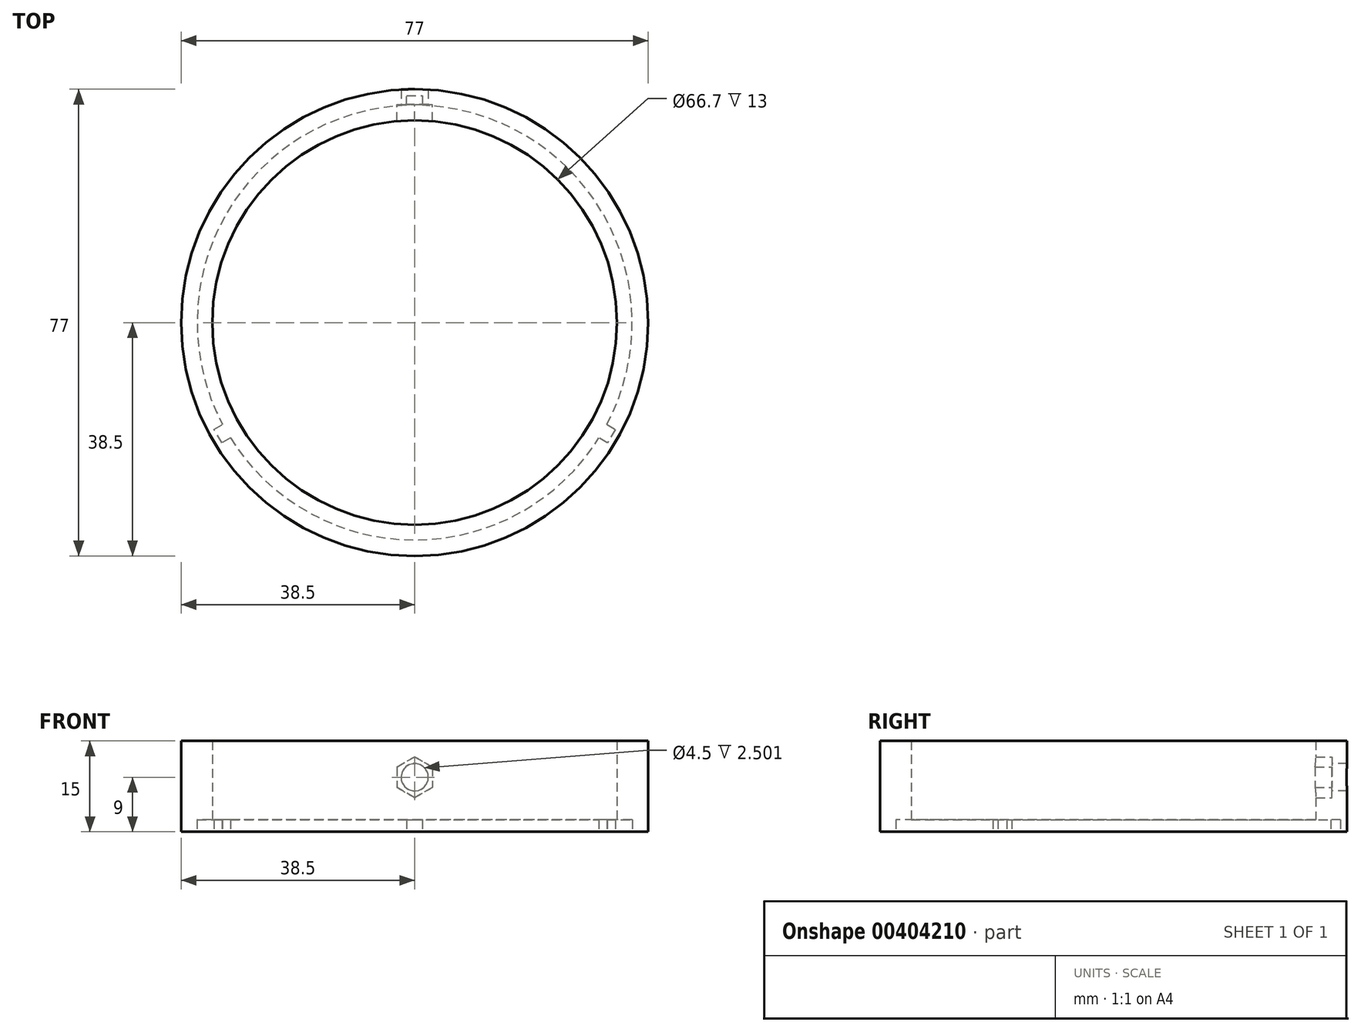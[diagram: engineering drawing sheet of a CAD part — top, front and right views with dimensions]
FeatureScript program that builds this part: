
annotation { "Feature Type Name" : "Feature", "Feature Type Description" : "" }
export const myFeature = defineFeature(function(context is Context, id is Id, definition is map)
    precondition{}
    {
        {
            var Q0;
            Q0=qCreatedBy(makeId("Top.planeOp"),FACE);
            var sketch = newSketch(context, id + "F0", { "sketchPlane" : qUnion([Q0])});
            skCircle(sketch, "E0", {"center": v(0, 0) * mm, "radius": 33.35 * mm});
            skCircle(sketch, "E1", {"center": v(0, 0) * mm, "radius": 38.5 * mm});
            skSolve(sketch);
        }
        {
            var Q0;
            Q0=qSketchRegion(id+"F0",true);
            extrude(context, id + "F1", {"entities" : qUnion([Q0]), "depth" : 15 * mm});
        }
        {
            var Q0;
            Q0=qCreatedBy(makeId("Front.planeOp"),FACE);
            var sketch = newSketch(context, id + "F2", { "sketchPlane" : qUnion([Q0])});
            skCircle(sketch, "E2", {"center": v(0, 9) * mm, "radius": 2.25 * mm});
            skSolve(sketch);
        }
        {
            var Q0;
            Q0=qSketchRegion(id+"F2",true);
            extrude(context, id + "F3", {"entities" : qUnion([Q0]), "operationType" : NewBodyOperationType.REMOVE, "endBound" : BoundingType.THROUGH_ALL, "oppositeDirection" : true, "depth" : 25 * mm});
        }
        {
            var Q0;
            Q0=qCreatedBy(makeId("Front.planeOp"),FACE);
            cPlane(context, id + "F4", {"entities" : qUnion([Q0]), "cplaneType" : CPlaneType.OFFSET, "offset" : 36 * mm, "oppositeDirection" : true, "width" : 150 * mm, "height" : 150 * mm});
        }
        {
            var Q0;
            Q0=qCreatedBy(id+"F4.planeOp",FACE);
            var sketch = newSketch(context, id + "F5", { "sketchPlane" : qUnion([Q0])});
            skCircle(sketch, "E3.cCircle", {"center": v(0, 9) * mm, "radius": 2.92 * mm, "construction": true});
            skLineSegment(sketch, "E3.0", {"start": v(2.92, 10.68) * mm, "end": v(2.92, 7.32) * mm});
            skLineSegment(sketch, "E3.1", {"start": v(2.92, 7.32) * mm, "end": v(0, 5.63) * mm});
            skLineSegment(sketch, "E3.2", {"start": v(0, 5.63) * mm, "end": v(-2.92, 7.32) * mm});
            skLineSegment(sketch, "E3.3", {"start": v(-2.92, 7.32) * mm, "end": v(-2.92, 10.68) * mm});
            skLineSegment(sketch, "E3.4", {"start": v(-2.92, 10.68) * mm, "end": v(0, 12.37) * mm});
            skLineSegment(sketch, "E3.5", {"start": v(0, 12.37) * mm, "end": v(2.92, 10.68) * mm});
            skPoint(sketch, "E3.0.midPoint", {"position": v(2.92, 9) * mm});
            skSolve(sketch);
        }
        {
            var Q0;
            Q0=qSketchRegion(id+"F5",true);
            extrude(context, id + "F6", {"entities" : qUnion([Q0]), "operationType" : NewBodyOperationType.REMOVE, "depth" : 4 * mm});
        }
        {
            var Q0;
            Q0=makeQuery(id+"F1.opExtrude","CAP_FACE",FACE,{"disambiguationData":[OSD([sQuery(id+"F0.wireOp",EDGE,"E0"),sQuery(id+"F0.wireOp",EDGE,"E1")])],"isStart":false});
            var sketch = newSketch(context, id + "F7", { "sketchPlane" : qUnion([Q0])});
            skCircle(sketch, "E4", {"center": v(0, 0) * mm, "radius": 33.35 * mm});
            skArc(sketch, "E5", {"start": v(-0.8, 35.34) * mm, "mid": v(-30.61, 17.68) * mm, "end": v(-31, -16.98) * mm});
            skLineSegment(sketch, "E6", {"start": v(-0.8, 35.34) * mm, "end": v(-0.8, 36.94) * mm});
            skLineSegment(sketch, "E7.MirrorCS", {"start": v(0.8, 35.34) * mm, "end": v(0.8, 36.94) * mm});
            skLineSegment(sketch, "E8", {"start": v(-0.8, 36.94) * mm, "end": v(0.8, 36.94) * mm});
            skLineSegment(sketch, "E9.1.0", {"start": v(-30.2, -18.36) * mm, "end": v(-31.6, -19.16) * mm});
            skLineSegment(sketch, "E9.1.1", {"start": v(-31.6, -19.16) * mm, "end": v(-32.4, -17.78) * mm});
            skLineSegment(sketch, "E9.1.2", {"start": v(-31, -16.98) * mm, "end": v(-32.4, -17.78) * mm});
            skLineSegment(sketch, "E9.2.0", {"start": v(31, -16.98) * mm, "end": v(32.4, -17.78) * mm});
            skLineSegment(sketch, "E9.2.1", {"start": v(32.4, -17.78) * mm, "end": v(31.6, -19.16) * mm});
            skLineSegment(sketch, "E9.2.2", {"start": v(30.2, -18.36) * mm, "end": v(31.6, -19.16) * mm});
            skArc(sketch, "E10.trimOffspring", {"start": v(-30.2, -18.36) * mm, "mid": v(0, -35.35) * mm, "end": v(30.2, -18.36) * mm});
            skArc(sketch, "E11.trimOffspring", {"start": v(31, -16.98) * mm, "mid": v(30.61, 17.67) * mm, "end": v(0.8, 35.34) * mm});
            skSolve(sketch);
        }
        {
            var Q0;
            Q0=qSketchRegion(id+"F7",true);
            extrude(context, id + "F8", {"entities" : qUnion([Q0]), "operationType" : NewBodyOperationType.ADD, "depth" : 2 * mm});
        }
        {
            var Q0;
            Q0=qCreatedBy(makeId("Top.planeOp"),FACE);
            var sketch = newSketch(context, id + "F9", { "sketchPlane" : qUnion([Q0])});
            skArc(sketch, "E12", {"start": v(-1.3, 35.83) * mm, "mid": v(-31.05, 17.93) * mm, "end": v(-31.68, -16.79) * mm});
            skLineSegment(sketch, "E13", {"start": v(-1.3, 35.83) * mm, "end": v(-1.3, 37.44) * mm});
            skLineSegment(sketch, "E14", {"start": v(-1.3, 37.44) * mm, "end": v(1.3, 37.44) * mm});
            skLineSegment(sketch, "E15", {"start": v(1.3, 37.44) * mm, "end": v(1.3, 35.83) * mm});
            skLineSegment(sketch, "E16.1.0", {"start": v(-30.38, -19.04) * mm, "end": v(-31.77, -19.85) * mm});
            skLineSegment(sketch, "E16.1.1", {"start": v(-31.77, -19.85) * mm, "end": v(-33.07, -17.6) * mm});
            skLineSegment(sketch, "E16.1.2", {"start": v(-33.07, -17.6) * mm, "end": v(-31.68, -16.79) * mm});
            skLineSegment(sketch, "E16.2.0", {"start": v(31.68, -16.79) * mm, "end": v(33.07, -17.6) * mm});
            skLineSegment(sketch, "E16.2.1", {"start": v(33.07, -17.6) * mm, "end": v(31.77, -19.85) * mm});
            skLineSegment(sketch, "E16.2.2", {"start": v(31.77, -19.85) * mm, "end": v(30.38, -19.04) * mm});
            skArc(sketch, "E17.trimOffspring", {"start": v(31.68, -16.79) * mm, "mid": v(31.05, 17.92) * mm, "end": v(1.3, 35.83) * mm});
            skArc(sketch, "E18.trimOffspring", {"start": v(-30.38, -19.04) * mm, "mid": v(0, -35.85) * mm, "end": v(30.38, -19.04) * mm});
            skSolve(sketch);
        }
        {
            var Q0;
            Q0=qSketchRegion(id+"F9",true);
            extrude(context, id + "F10", {"entities" : qUnion([Q0]), "operationType" : NewBodyOperationType.REMOVE, "depth" : 2 * mm});
        }
        {
            var Q0;
            Q0=makeQuery(id+"F1.opExtrude","CAP_FACE",FACE,{"disambiguationData":[OSD([sQuery(id+"F0.wireOp",EDGE,"E0"),sQuery(id+"F0.wireOp",EDGE,"E1")])],"isStart":false});
            var sketch = newSketch(context, id + "F11", { "sketchPlane" : qUnion([Q0])});
            skCircle(sketch, "E19", {"center": v(0, 0) * mm, "radius": 38.5 * mm});
            skSolve(sketch);
        }
        {
            var Q0;
            Q0 = qSketchRegion(id + "F11", true);
            extrude(context, id + "F12", {"entities" : qUnion([Q0]), "operationType" : NewBodyOperationType.REMOVE, "endBound" : BoundingType.THROUGH_ALL, "depth" : 25 * mm});
        }
    });
